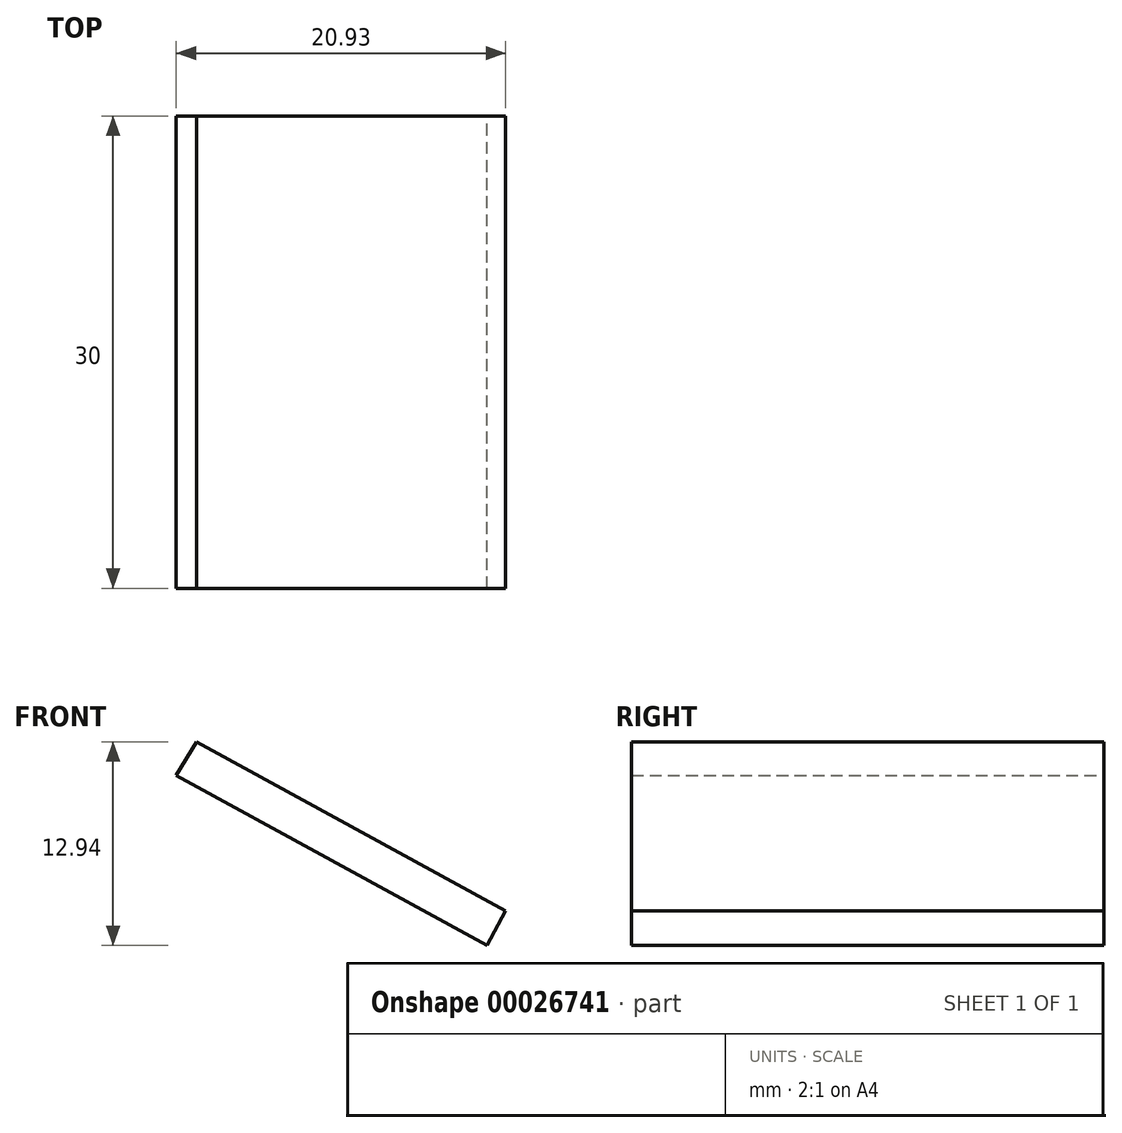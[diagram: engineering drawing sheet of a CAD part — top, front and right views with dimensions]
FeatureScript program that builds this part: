
annotation { "Feature Type Name" : "Feature", "Feature Type Description" : "" }
export const myFeature = defineFeature(function(context is Context, id is Id, definition is map)
    precondition{}
    {
        {
            var Q0;
            Q0=qCreatedBy(makeId("Front.planeOp"),FACE);
            var sketch = newSketch(context, id + "F0", { "sketchPlane" : qUnion([Q0])});
            skLineSegment(sketch, "E0", {"start": v(-22.6, 12.94) * mm, "end": v(-2.97, 2.2) * mm});
            skLineSegment(sketch, "E1", {"start": v(-2.97, 2.2) * mm, "end": v(-4.17, 0) * mm});
            skLineSegment(sketch, "E2", {"start": v(-4.17, 0) * mm, "end": v(-23.9, 10.8) * mm});
            skLineSegment(sketch, "E3", {"start": v(-23.9, 10.8) * mm, "end": v(-22.6, 12.94) * mm});
            skSolve(sketch);
        }
        {
            var Q0;
            Q0 = qSketchRegion(id + "F0", true);
            extrude(context, id + "F1", {"entities" : qUnion([Q0]), "depth" : 30 * mm});
        }
    });
